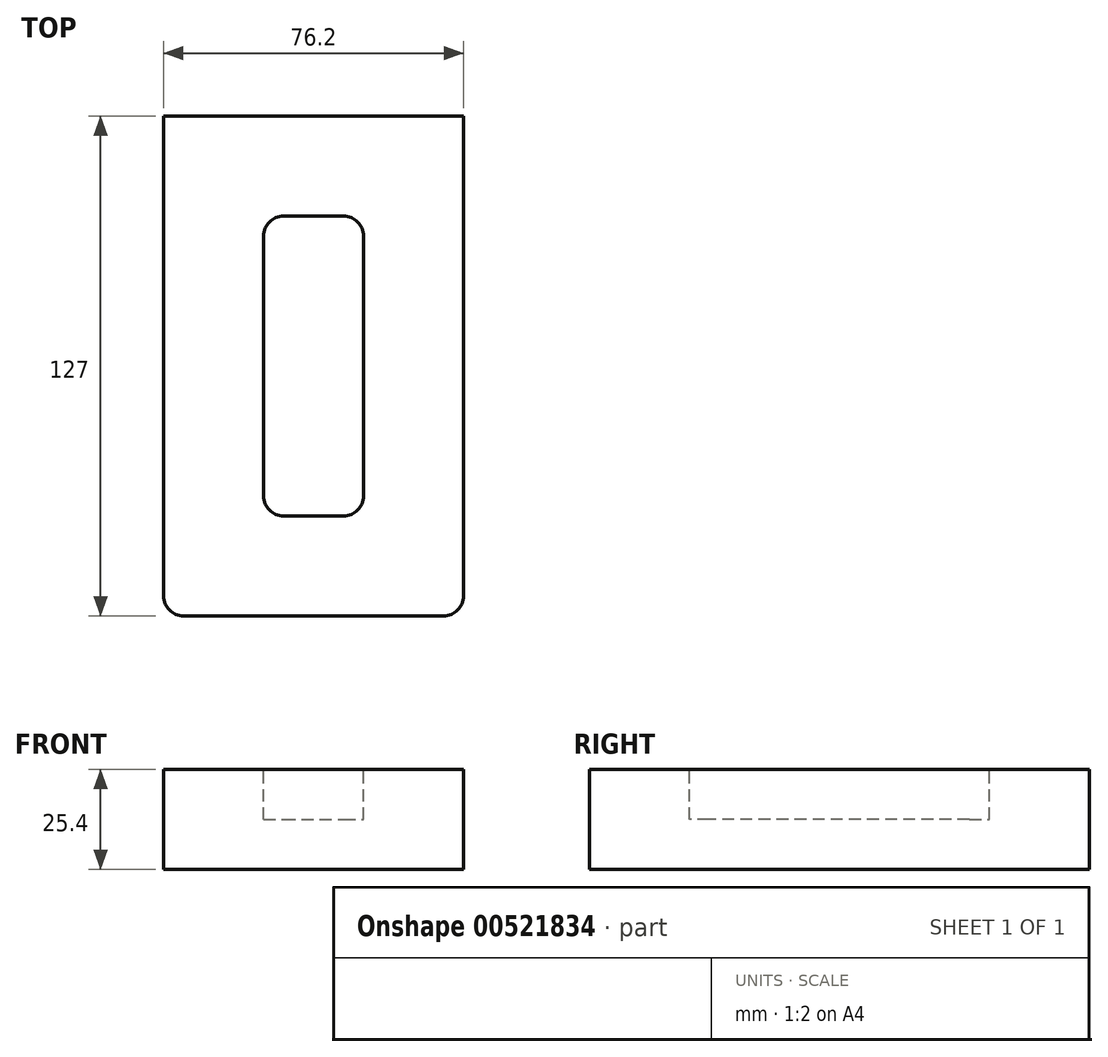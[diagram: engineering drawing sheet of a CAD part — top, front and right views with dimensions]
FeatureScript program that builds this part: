
annotation { "Feature Type Name" : "Feature", "Feature Type Description" : "" }
export const myFeature = defineFeature(function(context is Context, id is Id, definition is map)
    precondition{}
    {
        {
            var Q0;
            Q0=qCreatedBy(makeId("Top.planeOp"),FACE);
            var sketch = newSketch(context, id + "F0", { "sketchPlane" : qUnion([Q0])});
            skLineSegment(sketch, "E0.bottom", {"start": v(0, 0) * mm, "end": v(76.2, 0) * mm});
            skLineSegment(sketch, "E0.top", {"start": v(0, -127) * mm, "end": v(76.2, -127) * mm});
            skLineSegment(sketch, "E0.left", {"start": v(0, 0) * mm, "end": v(0, -127) * mm});
            skLineSegment(sketch, "E0.right", {"start": v(76.2, 0) * mm, "end": v(76.2, -127) * mm});
            skSolve(sketch);
        }
        {
            var Q0;
            Q0=makeQuery(id+"F0.imprint","IMPRINT",FACE,{"disambiguationData":[TD([[makeQuery(id+"F0.imprint","IMPRINT",EDGE,{"derivedFrom":sQuery(id+"F0.wireOp",EDGE,"E0.bottom")}),-1.0]])]});
            extrude(context, id + "F1", {"entities" : qUnion([Q0]), "depth" : 25.4 * mm, "offsetDistance" : 25.4 * mm});
        }
        {
            var Q0;
            Q0=makeQuery(id+"F1.opExtrude","SWEPT_EDGE",EDGE,{"disambiguationData":[OSD([sQuery(id+"F0.wireOp",EDGE,"E0.top"),sQuery(id+"F0.wireOp",EDGE,"E0.left")])]});
            var Q1;
            Q1=makeQuery(id+"F1.opExtrude","SWEPT_EDGE",EDGE,{"disambiguationData":[OSD([sQuery(id+"F0.wireOp",EDGE,"E0.top"),sQuery(id+"F0.wireOp",EDGE,"E0.right")])]});
            fillet(context, id + "F2", {"entities" : qUnion([Q0, Q1]), "radius" : 5.08 * mm, "tangentPropagation" : true, "allowEdgeOverflow" : false});
        }
        {
            var Q0;
            Q0=makeQuery(id+"F1.opExtrude","CAP_FACE",FACE,{"disambiguationData":[OSD([sQuery(id+"F0.wireOp",EDGE,"E0.bottom"),sQuery(id+"F0.wireOp",EDGE,"E0.top"),sQuery(id+"F0.wireOp",EDGE,"E0.left"),sQuery(id+"F0.wireOp",EDGE,"E0.right")])],"isStart":false});
            var sketch = newSketch(context, id + "F3", { "sketchPlane" : qUnion([Q0])});
            skLineSegment(sketch, "E1.bottom", {"start": v(25.4, -25.4) * mm, "end": v(50.8, -25.4) * mm});
            skLineSegment(sketch, "E1.top", {"start": v(25.4, -101.6) * mm, "end": v(50.8, -101.6) * mm});
            skLineSegment(sketch, "E1.left", {"start": v(25.4, -25.4) * mm, "end": v(25.4, -101.6) * mm});
            skLineSegment(sketch, "E1.right", {"start": v(50.8, -25.4) * mm, "end": v(50.8, -101.6) * mm});
            skSolve(sketch);
        }
        {
            var Q0;
            Q0 = qSketchRegion(id + "F3", true);
            extrude(context, id + "F4", {"entities" : qUnion([Q0]), "operationType" : NewBodyOperationType.REMOVE, "oppositeDirection" : true, "depth" : 12.7 * mm, "offsetDistance" : 25.4 * mm});
        }
        {
            var Q0;
            Q0=makeQuery(id+"F4.boolean.opBoolean","COPY",EDGE,{"derivedFrom":makeQuery(id+"F4.opExtrude","SWEPT_EDGE",EDGE,{"disambiguationData":[OSD([sQuery(id+"F3.wireOp",EDGE,"E1.bottom"),sQuery(id+"F3.wireOp",EDGE,"E1.right")])]})});
            var Q1;
            Q1=makeQuery(id+"F4.boolean.opBoolean","COPY",EDGE,{"derivedFrom":makeQuery(id+"F4.opExtrude","SWEPT_EDGE",EDGE,{"disambiguationData":[OSD([sQuery(id+"F3.wireOp",EDGE,"E1.bottom"),sQuery(id+"F3.wireOp",EDGE,"E1.left")])]})});
            var Q2;
            Q2=makeQuery(id+"F4.boolean.opBoolean","COPY",EDGE,{"derivedFrom":makeQuery(id+"F4.opExtrude","SWEPT_EDGE",EDGE,{"disambiguationData":[OSD([sQuery(id+"F3.wireOp",EDGE,"E1.top"),sQuery(id+"F3.wireOp",EDGE,"E1.right")])]})});
            var Q3;
            Q3=makeQuery(id+"F4.boolean.opBoolean","COPY",EDGE,{"derivedFrom":makeQuery(id+"F4.opExtrude","SWEPT_EDGE",EDGE,{"disambiguationData":[OSD([sQuery(id+"F3.wireOp",EDGE,"E1.top"),sQuery(id+"F3.wireOp",EDGE,"E1.left")])]})});
            fillet(context, id + "F5", {"entities" : qUnion([Q0, Q1, Q2, Q3]), "radius" : 5.08 * mm, "tangentPropagation" : true, "allowEdgeOverflow" : false});
        }
    });
